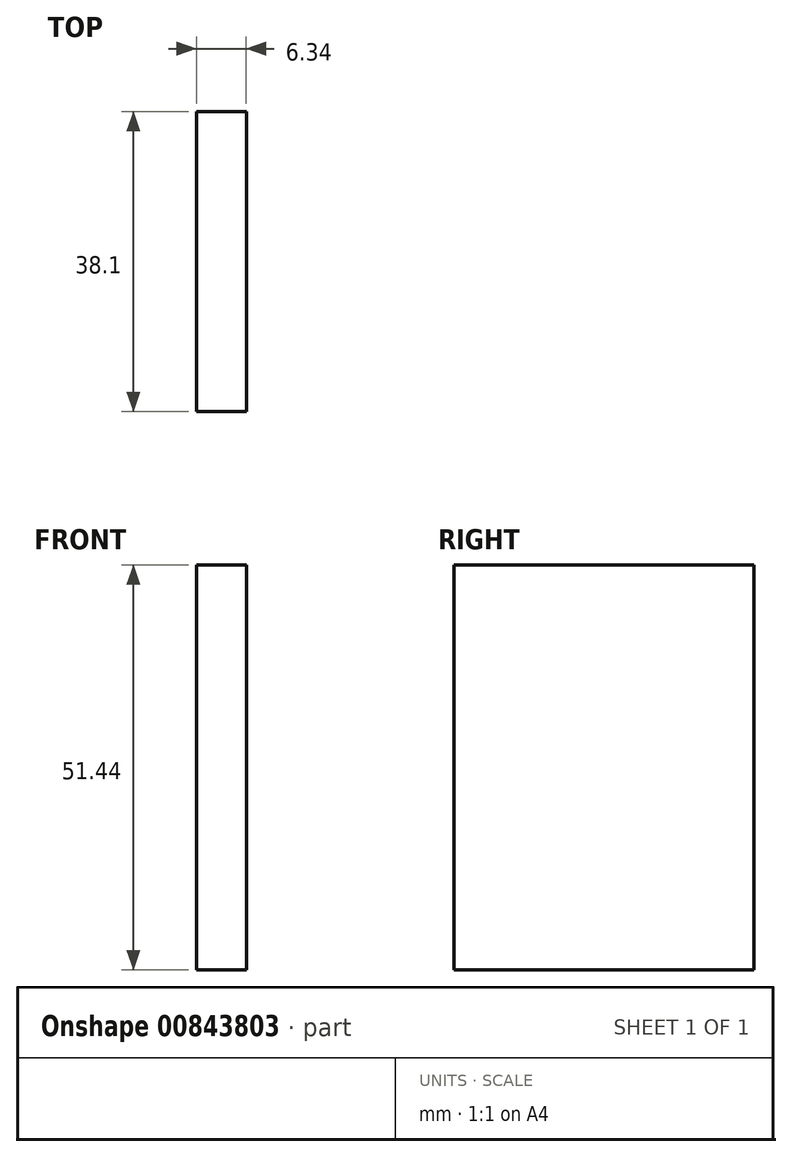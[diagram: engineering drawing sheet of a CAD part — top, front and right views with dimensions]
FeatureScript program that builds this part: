
annotation { "Feature Type Name" : "Feature", "Feature Type Description" : "" }
export const myFeature = defineFeature(function(context is Context, id is Id, definition is map)
    precondition{}
    {
        {
            var Q0;
            Q0=qCreatedBy(makeId("Front.planeOp"),FACE);
            var sketch = newSketch(context, id + "F0", { "sketchPlane" : qUnion([Q0])});
            skLineSegment(sketch, "E0.bottom", {"start": v(3.17, 25.72) * mm, "end": v(-3.18, 25.72) * mm});
            skLineSegment(sketch, "E0.top", {"start": v(3.18, -25.72) * mm, "end": v(-3.17, -25.72) * mm});
            skLineSegment(sketch, "E0.left", {"start": v(3.17, 25.72) * mm, "end": v(3.18, -25.72) * mm});
            skLineSegment(sketch, "E0.right", {"start": v(-3.18, 25.72) * mm, "end": v(-3.17, -25.72) * mm});
            skPoint(sketch, "E0.middle", {"position": v(0, 0) * mm});
            skSolve(sketch);
        }
        {
            var Q0;
            Q0 = qSketchRegion(id + "F0", true);
            extrude(context, id + "F1", {"entities" : qUnion([Q0]), "depth" : 38.1 * mm, "offsetDistance" : 25.4 * mm});
        }
    });
